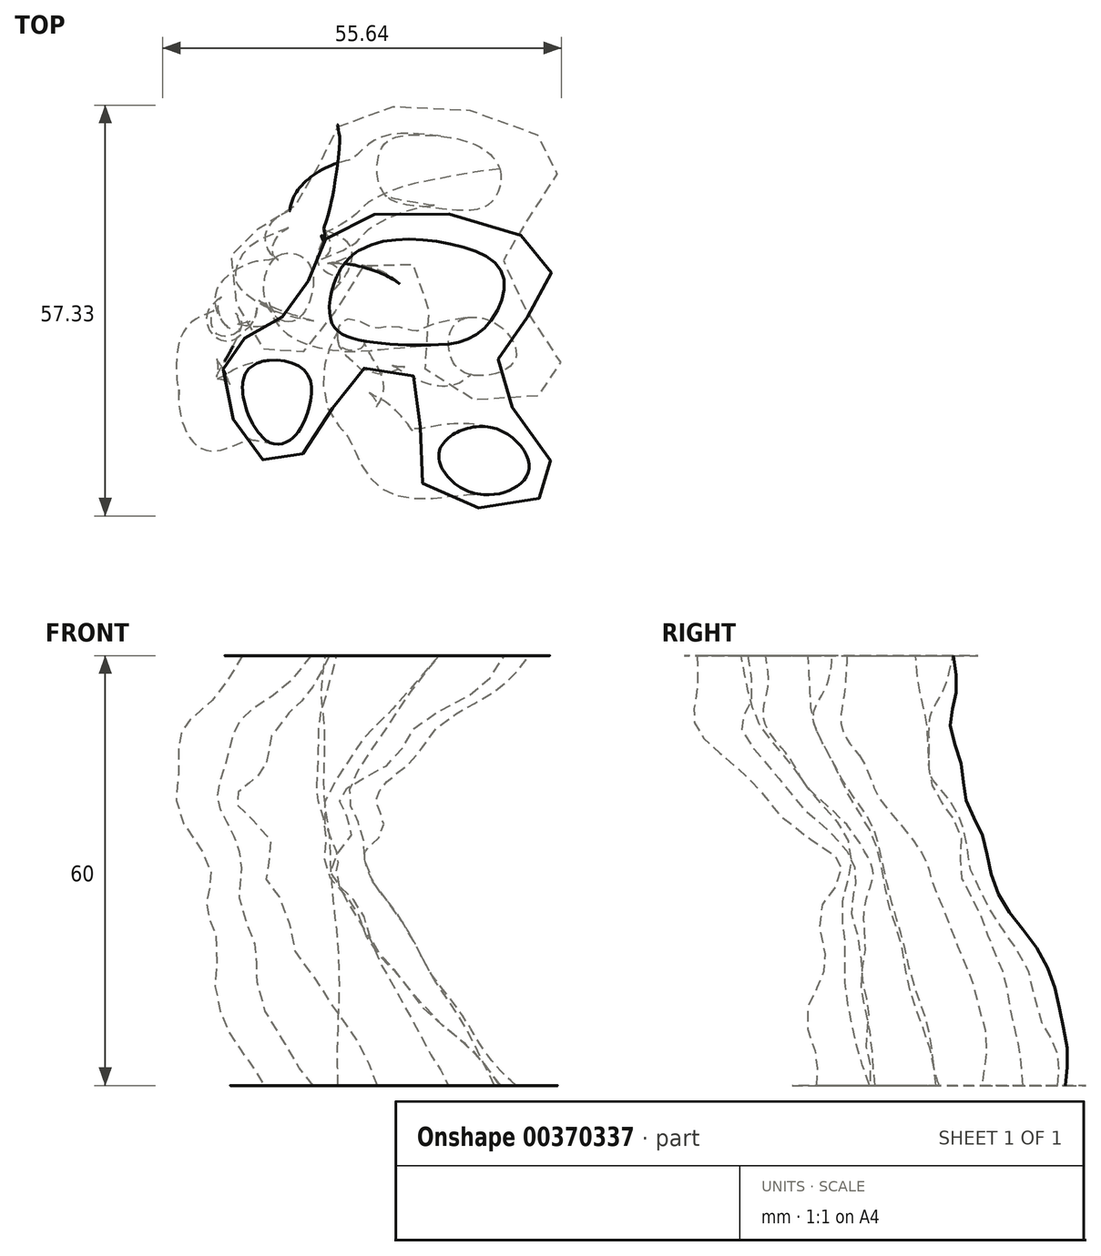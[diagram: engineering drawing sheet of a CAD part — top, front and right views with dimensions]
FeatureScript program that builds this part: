
annotation { "Feature Type Name" : "Feature", "Feature Type Description" : "" }
export const myFeature = defineFeature(function(context is Context, id is Id, definition is map)
    precondition{}
    {
        {
            var Q0;
            Q0=qCreatedBy(makeId("Top.planeOp"),FACE);
            cPlane(context, id + "F0", {"entities" : qUnion([Q0]), "cplaneType" : CPlaneType.OFFSET, "offset" : 5 * mm, "width" : 152.4 * mm, "height" : 152.4 * mm});
        }
        {
            var Q0;
            Q0=qCreatedBy(id+"F0.planeOp",FACE);
            var sketch = newSketch(context, id + "F1", { "sketchPlane" : qUnion([Q0])});
            skFitSpline(sketch, "E0", {"points": [v(-4.12, 24.5) * mm, v(12.71, 27.07) * mm, v(26.5, 20.1) * mm, v(22.26, 11.53) * mm, v(19.15, 3.69) * mm, v(26.98, -8.8) * mm, v(21.6, -13.7) * mm, v(8.13, -9.54) * mm, v(8.37, 3.2) * mm, v(0, 5.4) * mm, v(-6.08, -4.15) * mm, v(-12.69, -7.58) * mm, v(-18.32, 0) * mm, v(-18.32, 8.1) * mm, v(-12.69, 11.52) * mm, v(-7.54, 17.15) * mm, v(-4.12, 24.5) * mm]});
            skSolve(sketch);
        }
        {
            var Q0;
            Q0=qCreatedBy(id+"F0.planeOp",FACE);
            var sketch = newSketch(context, id + "F2", { "sketchPlane" : qUnion([Q0])});
            skFitSpline(sketch, "E1", {"points": [v(18.43, 18.57) * mm, v(16.76, 13.55) * mm, v(8.38, 13.27) * mm, v(2.23, 15.22) * mm, v(2.23, 21.92) * mm, v(8.1, 23.32) * mm, v(14.52, 22.2) * mm, v(18.43, 18.57) * mm]});
            skSolve(sketch);
        }
        {
            var Q0;
            Q0=qCreatedBy(id+"F0.planeOp",FACE);
            var sketch = newSketch(context, id + "F3", { "sketchPlane" : qUnion([Q0])});
            skFitSpline(sketch, "E2", {"points": [v(-12.55, 6.45) * mm, v(-8.36, 5.62) * mm, v(-8.08, 0.17) * mm, v(-10.88, -2.76) * mm, v(-14.23, 0.17) * mm, v(-12.55, 6.45) * mm]});
            skSolve(sketch);
        }
        {
            var Q0;
            Q0=qCreatedBy(id+"F0.planeOp",FACE);
            var sketch = newSketch(context, id + "F4", { "sketchPlane" : qUnion([Q0])});
            skFitSpline(sketch, "E3", {"points": [v(17.7, -2.86) * mm, v(20.7, -7.64) * mm, v(17.04, -10.13) * mm, v(12.22, -8.8) * mm, v(12.1, -3.14) * mm, v(17.7, -2.86) * mm]});
            skSolve(sketch);
        }
        {
            var Q0;
            Q0=qCreatedBy(id+"F0.planeOp",FACE);
            cPlane(context, id + "F5", {"entities" : qUnion([Q0]), "cplaneType" : CPlaneType.OFFSET, "offset" : 5 * mm, "width" : 152.4 * mm, "height" : 152.4 * mm});
        }
        {
            var Q0;
            Q0=qCreatedBy(id+"F5.planeOp",FACE);
            var sketch = newSketch(context, id + "F6", { "sketchPlane" : qUnion([Q0])});
            skFitSpline(sketch, "E4", {"points": [v(-7.05, 23.03) * mm, v(8.37, 25.24) * mm, v(21.1, 19.11) * mm, v(17.19, 11.52) * mm, v(14.74, 2.22) * mm, v(22.09, -9.05) * mm, v(17.19, -13.7) * mm, v(5.19, -10.27) * mm, v(5.43, 2.7) * mm, v(-3.38, 5.65) * mm, v(-10.48, -3.9) * mm, v(-16.85, -7.09) * mm, v(-20.77, 0) * mm, v(-20.28, 6.38) * mm, v(-14.9, 10.54) * mm, v(-10.48, 15.44) * mm, v(-7.05, 23.03) * mm]});
            skSolve(sketch);
        }
        {
            var Q0;
            Q0=qCreatedBy(id+"F5.planeOp",FACE);
            var sketch = newSketch(context, id + "F7", { "sketchPlane" : qUnion([Q0])});
            skFitSpline(sketch, "E5", {"points": [v(14.34, 18.87) * mm, v(13.14, 14.27) * mm, v(4.95, 14.07) * mm, v(0.15, 16.27) * mm, v(0, 21.86) * mm, v(7.15, 23.06) * mm, v(11.74, 21.66) * mm, v(14.34, 18.87) * mm]});
            skSolve(sketch);
        }
        {
            var Q0;
            Q0=qCreatedBy(id+"F5.planeOp",FACE);
            var sketch = newSketch(context, id + "F8", { "sketchPlane" : qUnion([Q0])});
            skFitSpline(sketch, "E6", {"points": [v(-16, 5.31) * mm, v(-11.56, 4.66) * mm, v(-12.52, -2) * mm, v(-15.68, -3.16) * mm, v(-17.67, 0) * mm, v(-16, 5.31) * mm]});
            skSolve(sketch);
        }
        {
            var Q0;
            Q0=qCreatedBy(id+"F5.planeOp",FACE);
            var sketch = newSketch(context, id + "F9", { "sketchPlane" : qUnion([Q0])});
            skFitSpline(sketch, "E7", {"points": [v(13.75, -3) * mm, v(16.15, -7.8) * mm, v(13.55, -10.39) * mm, v(9.07, -8.97) * mm, v(9.35, -3.6) * mm, v(13.75, -3) * mm]});
            skSolve(sketch);
        }
        {
            var Q0;
            Q0=qCreatedBy(id+"F5.planeOp",FACE);
            cPlane(context, id + "F10", {"entities" : qUnion([Q0]), "cplaneType" : CPlaneType.OFFSET, "offset" : 5 * mm, "width" : 152.4 * mm, "height" : 152.4 * mm});
        }
        {
            var Q0;
            Q0=qCreatedBy(id+"F10.planeOp",FACE);
            var sketch = newSketch(context, id + "F11", { "sketchPlane" : qUnion([Q0])});
            skFitSpline(sketch, "E8", {"points": [v(-8.03, 22.05) * mm, v(5.92, 23.28) * mm, v(15.47, 18.38) * mm, v(13.27, 11.03) * mm, v(11.56, 1) * mm, v(17.43, -8.8) * mm, v(13.02, -13.7) * mm, v(2.99, -10.76) * mm, v(3.47, 1.24) * mm, v(-4.85, 4.42) * mm, v(-12.2, -2.2) * mm, v(-17.83, -7.58) * mm, v(-21.5, -4.15) * mm, v(-22.73, 4.67) * mm, v(-17.58, 9.56) * mm, v(-12.2, 13.73) * mm, v(-8.03, 22.05) * mm]});
            skSolve(sketch);
        }
        {
            var Q0;
            Q0=qCreatedBy(id+"F10.planeOp",FACE);
            var sketch = newSketch(context, id + "F12", { "sketchPlane" : qUnion([Q0])});
            skFitSpline(sketch, "E9", {"points": [v(8.55, 15.27) * mm, v(6.55, 13.07) * mm, v(0, 13.07) * mm, v(-3.84, 15.47) * mm, v(-3.24, 19.27) * mm, v(2.75, 20.67) * mm, v(7.55, 19.07) * mm, v(8.55, 15.27) * mm]});
            skSolve(sketch);
        }
        {
            var Q0;
            Q0=qCreatedBy(id+"F10.planeOp",FACE);
            var sketch = newSketch(context, id + "F13", { "sketchPlane" : qUnion([Q0])});
            skFitSpline(sketch, "E10", {"points": [v(-19.66, 3.4) * mm, v(-15.66, 4.4) * mm, v(-14.46, -1) * mm, v(-18.17, -3) * mm, v(-20, -1.66) * mm, v(-19.66, 3.4) * mm]});
            skSolve(sketch);
        }
        {
            var Q0;
            Q0=qCreatedBy(id+"F10.planeOp",FACE);
            var sketch = newSketch(context, id + "F14", { "sketchPlane" : qUnion([Q0])});
            skFitSpline(sketch, "E11", {"points": [v(11.07, -3.7) * mm, v(13.06, -8.3) * mm, v(11.9, -11.3) * mm, v(6.9, -10.3) * mm, v(6.67, -4.5) * mm, v(11.07, -3.7) * mm]});
            skSolve(sketch);
        }
        {
            var Q0;
            Q0=qCreatedBy(id+"F10.planeOp",FACE);
            cPlane(context, id + "F15", {"entities" : qUnion([Q0]), "cplaneType" : CPlaneType.OFFSET, "offset" : 5 * mm, "width" : 152.4 * mm, "height" : 152.4 * mm});
        }
        {
            var Q0;
            Q0=qCreatedBy(id+"F15.planeOp",FACE);
            var sketch = newSketch(context, id + "F16", { "sketchPlane" : qUnion([Q0])});
            skFitSpline(sketch, "E12", {"points": [v(-9.5, 20.58) * mm, v(4.2, 21.8) * mm, v(12.05, 16.17) * mm, v(8.86, 9.07) * mm, v(8.37, 0) * mm, v(14.74, -6.35) * mm, v(7.88, -11.99) * mm, v(0, -8.56) * mm, v(1.52, 0) * mm, v(-6.08, 3.69) * mm, v(-10.97, 0) * mm, v(-13.91, -4.64) * mm, v(-20.03, -6.84) * mm, v(-22.73, 3.93) * mm, v(-17.34, 7.85) * mm, v(-13.42, 12.5) * mm, v(-9.5, 20.58) * mm]});
            skSolve(sketch);
        }
        {
            var Q0;
            Q0=qCreatedBy(id+"F15.planeOp",FACE);
            var sketch = newSketch(context, id + "F17", { "sketchPlane" : qUnion([Q0])});
            skFitSpline(sketch, "E13", {"points": [v(4.75, 15.47) * mm, v(2.75, 11.68) * mm, v(-3.44, 12.08) * mm, v(-7.04, 14.07) * mm, v(-6.64, 18.07) * mm, v(-1.6, 19.66) * mm, v(2.55, 18.87) * mm, v(4.75, 15.47) * mm]});
            skSolve(sketch);
        }
        {
            var Q0;
            Q0=qCreatedBy(id+"F15.planeOp",FACE);
            var sketch = newSketch(context, id + "F18", { "sketchPlane" : qUnion([Q0])});
            skFitSpline(sketch, "E14", {"points": [v(-20.9, 1.85) * mm, v(-16.93, 2.72) * mm, v(-15.5, -1.35) * mm, v(-17.3, -3.75) * mm, v(-20.1, -2.95) * mm, v(-20.9, 1.85) * mm]});
            skSolve(sketch);
        }
        {
            var Q0;
            Q0=qCreatedBy(id+"F15.planeOp",FACE);
            var sketch = newSketch(context, id + "F19", { "sketchPlane" : qUnion([Q0])});
            skFitSpline(sketch, "E15", {"points": [v(7.97, -4.39) * mm, v(9.17, -6.39) * mm, v(8.77, -8.58) * mm, v(3.78, -8.98) * mm, v(3.58, -4.99) * mm, v(7.97, -4.39) * mm]});
            skSolve(sketch);
        }
        {
            var Q0;
            Q0=qCreatedBy(id+"F15.planeOp",FACE);
            cPlane(context, id + "F20", {"entities" : qUnion([Q0]), "cplaneType" : CPlaneType.OFFSET, "offset" : 5 * mm, "width" : 152.4 * mm, "height" : 152.4 * mm});
        }
        {
            var Q0;
            Q0=qCreatedBy(id+"F20.planeOp",FACE);
            var sketch = newSketch(context, id + "F21", { "sketchPlane" : qUnion([Q0])});
            skFitSpline(sketch, "E16", {"points": [v(-13.18, 17.64) * mm, v(0, 19.11) * mm, v(6.66, 13.48) * mm, v(3.47, 8.58) * mm, v(4.2, 0) * mm, v(10.09, -5.37) * mm, v(7.64, -10.03) * mm, v(0, -10.76) * mm, v(-2.4, -1.95) * mm, v(-8.03, 0) * mm, v(-12.69, -1.95) * mm, v(-14.4, -5.86) * mm, v(-17.83, -8.31) * mm, v(-22.24, -3.41) * mm, v(-21.5, 4.18) * mm, v(-15.87, 9.8) * mm, v(-13.18, 17.64) * mm]});
            skSolve(sketch);
        }
        {
            var Q0;
            Q0=qCreatedBy(id+"F20.planeOp",FACE);
            var sketch = newSketch(context, id + "F22", { "sketchPlane" : qUnion([Q0])});
            skFitSpline(sketch, "E17", {"points": [v(0, 14.47) * mm, v(0, 10.08) * mm, v(-5.44, 9.48) * mm, v(-10.03, 11.48) * mm, v(-10.23, 14.87) * mm, v(-6.84, 16.87) * mm, v(-3.44, 16.67) * mm, v(0, 14.47) * mm]});
            skSolve(sketch);
        }
        {
            var Q0;
            Q0=qCreatedBy(id+"F20.planeOp",FACE);
            var sketch = newSketch(context, id + "F23", { "sketchPlane" : qUnion([Q0])});
            skFitSpline(sketch, "E18", {"points": [v(-20.77, 0.14) * mm, v(-17.77, 1.83) * mm, v(-15.78, -1.37) * mm, v(-17.57, -4.17) * mm, v(-19.77, -3.57) * mm, v(-20.77, 0.14) * mm]});
            skSolve(sketch);
        }
        {
            var Q0;
            Q0=qCreatedBy(id+"F20.planeOp",FACE);
            var sketch = newSketch(context, id + "F24", { "sketchPlane" : qUnion([Q0])});
            skFitSpline(sketch, "E19", {"points": [v(4.46, -3.62) * mm, v(6.46, -5.62) * mm, v(5.08, -8.97) * mm, v(1.46, -8.41) * mm, v(1.07, -4.22) * mm, v(4.46, -3.62) * mm]});
            skSolve(sketch);
        }
        {
            var Q0;
            Q0=qCreatedBy(id+"F20.planeOp",FACE);
            cPlane(context, id + "F25", {"entities" : qUnion([Q0]), "cplaneType" : CPlaneType.OFFSET, "offset" : 5 * mm, "width" : 152.4 * mm, "height" : 152.4 * mm});
        }
        {
            var Q0;
            Q0=qCreatedBy(id+"F25.planeOp",FACE);
            var sketch = newSketch(context, id + "F26", { "sketchPlane" : qUnion([Q0])});
            skFitSpline(sketch, "E20", {"points": [v(-12.82, 14.5) * mm, v(-2.24, 15.58) * mm, v(3.73, 10.96) * mm, v(0, 5.8) * mm, v(0, 0) * mm, v(6.45, -5.86) * mm, v(4.82, -10.74) * mm, v(-2.5, -11.29) * mm, v(-5.5, -3.15) * mm, v(-10.65, 0) * mm, v(-15.53, -3.15) * mm, v(-15.8, -6.4) * mm, v(-20.14, -8.03) * mm, v(-25.57, 0) * mm, v(-23.13, 2.82) * mm, v(-15.3, 8.02) * mm, v(-12.82, 14.5) * mm]});
            skSolve(sketch);
        }
        {
            var Q0;
            Q0=qCreatedBy(id+"F25.planeOp",FACE);
            var sketch = newSketch(context, id + "F27", { "sketchPlane" : qUnion([Q0])});
            skFitSpline(sketch, "E21", {"points": [v(-1.64, 11.88) * mm, v(-2.04, 8.08) * mm, v(-7.44, 7.68) * mm, v(-11.03, 9.48) * mm, v(-11.03, 12.67) * mm, v(-8.04, 13.67) * mm, v(-4.64, 13.07) * mm, v(-1.64, 11.88) * mm]});
            skSolve(sketch);
        }
        {
            var Q0;
            Q0=qCreatedBy(id+"F25.planeOp",FACE);
            var sketch = newSketch(context, id + "F28", { "sketchPlane" : qUnion([Q0])});
            skFitSpline(sketch, "E22", {"points": [v(-22.4, -1.58) * mm, v(-19.8, 0.41) * mm, v(-18, -1.78) * mm, v(-18.33, -4.99) * mm, v(-21, -4.99) * mm, v(-22.4, -1.58) * mm]});
            skSolve(sketch);
        }
        {
            var Q0;
            Q0=qCreatedBy(id+"F25.planeOp",FACE);
            var sketch = newSketch(context, id + "F29", { "sketchPlane" : qUnion([Q0])});
            skFitSpline(sketch, "E23", {"points": [v(1.34, -3.72) * mm, v(3.34, -6.92) * mm, v(2.34, -9.12) * mm, v(-1.44, -8.98) * mm, v(-2.06, -4.92) * mm, v(1.34, -3.72) * mm]});
            skSolve(sketch);
        }
        {
            var Q0;
            Q0=qCreatedBy(id+"F25.planeOp",FACE);
            cPlane(context, id + "F30", {"entities" : qUnion([Q0]), "cplaneType" : CPlaneType.OFFSET, "offset" : 5 * mm, "width" : 152.4 * mm, "height" : 152.4 * mm});
        }
        {
            var Q0;
            Q0=qCreatedBy(id+"F30.planeOp",FACE);
            var sketch = newSketch(context, id + "F31", { "sketchPlane" : qUnion([Q0])});
            skFitSpline(sketch, "E24", {"points": [v(-15.83, 12.08) * mm, v(-5.64, 14.07) * mm, v(0, 10.48) * mm, v(-2.24, 4.68) * mm, v(-1.84, 0) * mm, v(2.95, -4.5) * mm, v(2.35, -7.1) * mm, v(-5.44, -8.1) * mm, v(-6.84, 0) * mm, v(-11.23, 1.69) * mm, v(-15.23, -1.9) * mm, v(-15.83, -6.3) * mm, v(-20.62, -7.5) * mm, v(-23.82, -2.3) * mm, v(-23.02, 2.29) * mm, v(-18.02, 7.28) * mm, v(-15.83, 12.08) * mm]});
            skSolve(sketch);
        }
        {
            var Q0;
            Q0=qCreatedBy(id+"F30.planeOp",FACE);
            var sketch = newSketch(context, id + "F32", { "sketchPlane" : qUnion([Q0])});
            skFitSpline(sketch, "E25", {"points": [v(-6.24, 10.48) * mm, v(-5.44, 6.88) * mm, v(-9.83, 5.48) * mm, v(-13.43, 6.68) * mm, v(-14.23, 9.08) * mm, v(-12.63, 10.88) * mm, v(-8.84, 11.28) * mm, v(-6.24, 10.48) * mm]});
            skSolve(sketch);
        }
        {
            var Q0;
            Q0=qCreatedBy(id+"F30.planeOp",FACE);
            var sketch = newSketch(context, id + "F33", { "sketchPlane" : qUnion([Q0])});
            skFitSpline(sketch, "E26", {"points": [v(-21.53, -1.24) * mm, v(-18.93, -1.24) * mm, v(-17.53, -3.03) * mm, v(-18.53, -4.43) * mm, v(-21.13, -4.43) * mm, v(-21.53, -1.24) * mm]});
            skSolve(sketch);
        }
        {
            var Q0;
            Q0=qCreatedBy(id+"F30.planeOp",FACE);
            var sketch = newSketch(context, id + "F34", { "sketchPlane" : qUnion([Q0])});
            skFitSpline(sketch, "E27", {"points": [v(-2.64, -2.35) * mm, v(0, -4.55) * mm, v(-1.04, -6.55) * mm, v(-3.84, -6.15) * mm, v(-4.24, -3.95) * mm, v(-2.64, -2.35) * mm]});
            skSolve(sketch);
        }
        {
            var Q0;
            Q0=qCreatedBy(id+"F30.planeOp",FACE);
            cPlane(context, id + "F35", {"entities" : qUnion([Q0]), "cplaneType" : CPlaneType.OFFSET, "offset" : 5 * mm, "width" : 152.4 * mm, "height" : 152.4 * mm});
        }
        {
            var Q0;
            Q0=qCreatedBy(id+"F35.planeOp",FACE);
            var sketch = newSketch(context, id + "F36", { "sketchPlane" : qUnion([Q0])});
            skFitSpline(sketch, "E28", {"points": [v(-14.78, 11.48) * mm, v(-4.2, 12.57) * mm, v(1.77, 7.96) * mm, v(-1.97, 2.8) * mm, v(-1.97, -3) * mm, v(4.48, -8.87) * mm, v(2.85, -13.75) * mm, v(-4.47, -14.3) * mm, v(-7.46, -6.15) * mm, v(-12.61, -3) * mm, v(-17.5, -6.15) * mm, v(-17.77, -9.4) * mm, v(-22.11, -11.04) * mm, v(-27.54, -3) * mm, v(-25.1, -0.18) * mm, v(-17.27, 5.01) * mm, v(-14.78, 11.48) * mm]});
            skSolve(sketch);
        }
        {
            var Q0;
            Q0=qCreatedBy(id+"F35.planeOp",FACE);
            var sketch = newSketch(context, id + "F37", { "sketchPlane" : qUnion([Q0])});
            skFitSpline(sketch, "E29", {"points": [v(-2.27, 7.4) * mm, v(-4.04, 3.54) * mm, v(-9.01, 2.74) * mm, v(-12.86, 4.02) * mm, v(-13.98, 6.75) * mm, v(-12.06, 9.96) * mm, v(-5.48, 9.8) * mm, v(-2.27, 7.4) * mm]});
            skSolve(sketch);
        }
        {
            var Q0;
            Q0=qCreatedBy(id+"F35.planeOp",FACE);
            var sketch = newSketch(context, id + "F38", { "sketchPlane" : qUnion([Q0])});
            skFitSpline(sketch, "E30", {"points": [v(-24.32, -2.67) * mm, v(-19.66, -2.67) * mm, v(-18.7, -4.92) * mm, v(-19.57, -7.32) * mm, v(-23.03, -7.32) * mm, v(-24.32, -2.67) * mm]});
            skSolve(sketch);
        }
        {
            var Q0;
            Q0=qCreatedBy(id+"F35.planeOp",FACE);
            var sketch = newSketch(context, id + "F39", { "sketchPlane" : qUnion([Q0])});
            skFitSpline(sketch, "E31", {"points": [v(-2.5, -4.98) * mm, v(0.23, -7.25) * mm, v(1.7, -11.1) * mm, v(-3.03, -11.45) * mm, v(-5.13, -6.03) * mm, v(-2.5, -4.98) * mm]});
            skSolve(sketch);
        }
        {
            var Q0;
            Q0=qCreatedBy(id+"F35.planeOp",FACE);
            cPlane(context, id + "F40", {"entities" : qUnion([Q0]), "cplaneType" : CPlaneType.OFFSET, "offset" : 5 * mm, "width" : 152.4 * mm, "height" : 152.4 * mm});
        }
        {
            var Q0;
            Q0=qCreatedBy(id+"F40.planeOp",FACE);
            var sketch = newSketch(context, id + "F41", { "sketchPlane" : qUnion([Q0])});
            skFitSpline(sketch, "E32", {"points": [v(-18.89, 9) * mm, v(-5.71, 10.47) * mm, v(0.94, 4.84) * mm, v(-2.24, -0.06) * mm, v(-1.5, -8.65) * mm, v(4.37, -14.02) * mm, v(1.92, -18.67) * mm, v(-5.71, -19.4) * mm, v(-8.12, -10.6) * mm, v(-13.75, -8.65) * mm, v(-18.4, -10.6) * mm, v(-20.11, -14.5) * mm, v(-23.54, -16.96) * mm, v(-27.95, -12.06) * mm, v(-27.22, -4.47) * mm, v(-21.58, 1.16) * mm, v(-18.89, 9) * mm]});
            skSolve(sketch);
        }
        {
            var Q0;
            Q0=qCreatedBy(id+"F40.planeOp",FACE);
            var sketch = newSketch(context, id + "F42", { "sketchPlane" : qUnion([Q0])});
            skFitSpline(sketch, "E33", {"points": [v(-3.97, 4.35) * mm, v(-5.9, 0) * mm, v(-11.84, -1.25) * mm, v(-17.44, 1.72) * mm, v(-18.49, 3.82) * mm, v(-16.39, 7.5) * mm, v(-8.69, 7.5) * mm, v(-3.97, 4.35) * mm]});
            skSolve(sketch);
        }
        {
            var Q0;
            Q0=qCreatedBy(id+"F40.planeOp",FACE);
            var sketch = newSketch(context, id + "F43", { "sketchPlane" : qUnion([Q0])});
            skFitSpline(sketch, "E34", {"points": [v(-25.83, -5.62) * mm, v(-21.98, -5.62) * mm, v(-20.93, -9.47) * mm, v(-22.33, -12.8) * mm, v(-25.48, -12.8) * mm, v(-25.83, -5.62) * mm]});
            skSolve(sketch);
        }
        {
            var Q0;
            Q0=qCreatedBy(id+"F40.planeOp",FACE);
            var sketch = newSketch(context, id + "F44", { "sketchPlane" : qUnion([Q0])});
            skFitSpline(sketch, "E35", {"points": [v(-3.1, -10) * mm, v(1.28, -14.54) * mm, v(-2.4, -17.17) * mm, v(-5.37, -15.24) * mm, v(-5.37, -10.7) * mm, v(-3.1, -10) * mm]});
            skSolve(sketch);
        }
        {
            var Q0;
            Q0=qCreatedBy(id+"F40.planeOp",FACE);
            cPlane(context, id + "F45", {"entities" : qUnion([Q0]), "cplaneType" : CPlaneType.OFFSET, "offset" : 5 * mm, "width" : 152.4 * mm, "height" : 152.4 * mm});
        }
        {
            var Q0;
            Q0=qCreatedBy(id+"F45.planeOp",FACE);
            var sketch = newSketch(context, id + "F46", { "sketchPlane" : qUnion([Q0])});
            skFitSpline(sketch, "E36", {"points": [v(-14.52, 7.84) * mm, v(-0.8, 9.06) * mm, v(7.03, 3.43) * mm, v(3.84, -3.67) * mm, v(3.35, -12.75) * mm, v(9.72, -19.1) * mm, v(2.86, -24.73) * mm, v(-5.02, -21.3) * mm, v(-3.5, -12.75) * mm, v(-11.1, -9.06) * mm, v(-16, -12.75) * mm, v(-18.93, -17.38) * mm, v(-25.05, -19.59) * mm, v(-27.74, -8.81) * mm, v(-22.36, -4.9) * mm, v(-18.44, -0.24) * mm, v(-14.52, 7.84) * mm]});
            skSolve(sketch);
        }
        {
            var Q0;
            Q0=qCreatedBy(id+"F45.planeOp",FACE);
            var sketch = newSketch(context, id + "F47", { "sketchPlane" : qUnion([Q0])});
            skFitSpline(sketch, "E37", {"points": [v(3.03, 2.6) * mm, v(0, -2.82) * mm, v(-6.77, -3.35) * mm, v(-12.01, -2.3) * mm, v(-14.11, 1.55) * mm, v(-12.19, 4.17) * mm, v(-3.1, 5.4) * mm, v(3.03, 2.6) * mm]});
            skSolve(sketch);
        }
        {
            var Q0;
            Q0=qCreatedBy(id+"F45.planeOp",FACE);
            var sketch = newSketch(context, id + "F48", { "sketchPlane" : qUnion([Q0])});
            skFitSpline(sketch, "E38", {"points": [v(-25.13, -8.77) * mm, v(-20.58, -8.77) * mm, v(-19.88, -13.32) * mm, v(-21.28, -16.47) * mm, v(-25.13, -16.47) * mm, v(-25.13, -8.77) * mm]});
            skSolve(sketch);
        }
        {
            var Q0;
            Q0=qCreatedBy(id+"F45.planeOp",FACE);
            var sketch = newSketch(context, id + "F49", { "sketchPlane" : qUnion([Q0])});
            skFitSpline(sketch, "E39", {"points": [v(1.8, -13.67) * mm, v(5.83, -19.8) * mm, v(2.16, -22.07) * mm, v(-1.87, -20.32) * mm, v(-2.57, -15.94) * mm, v(1.8, -13.67) * mm]});
            skSolve(sketch);
        }
        {
            var Q0;
            Q0=qCreatedBy(id+"F45.planeOp",FACE);
            cPlane(context, id + "F50", {"entities" : qUnion([Q0]), "cplaneType" : CPlaneType.OFFSET, "offset" : 5 * mm, "width" : 152.4 * mm, "height" : 152.4 * mm});
        }
        {
            var Q0;
            Q0=qCreatedBy(id+"F50.planeOp",FACE);
            var sketch = newSketch(context, id + "F51", { "sketchPlane" : qUnion([Q0])});
            skFitSpline(sketch, "E40", {"points": [v(-12.26, 6.45) * mm, v(1.7, 7.68) * mm, v(11.25, 2.78) * mm, v(9.05, -4.57) * mm, v(7.33, -14.6) * mm, v(13.2, -24.4) * mm, v(8.8, -29.3) * mm, v(-1.24, -26.36) * mm, v(-0.75, -14.36) * mm, v(-9.07, -11.18) * mm, v(-16.42, -17.8) * mm, v(-22.05, -23.18) * mm, v(-25.73, -19.75) * mm, v(-26.95, -10.93) * mm, v(-21.8, -6.04) * mm, v(-16.42, -1.87) * mm, v(-12.26, 6.45) * mm]});
            skSolve(sketch);
        }
        {
            var Q0;
            Q0=qCreatedBy(id+"F50.planeOp",FACE);
            var sketch = newSketch(context, id + "F52", { "sketchPlane" : qUnion([Q0])});
            skFitSpline(sketch, "E41", {"points": [v(6.58, 0) * mm, v(4.42, -3.99) * mm, v(-2.06, -6.65) * mm, v(-10.03, -5.15) * mm, v(-12.85, -1.17) * mm, v(-8.54, 4.65) * mm, v(1.76, 4.15) * mm, v(6.58, 0) * mm]});
            skSolve(sketch);
        }
        {
            var Q0;
            Q0=qCreatedBy(id+"F50.planeOp",FACE);
            var sketch = newSketch(context, id + "F53", { "sketchPlane" : qUnion([Q0])});
            skFitSpline(sketch, "E42", {"points": [v(-24.98, -11.63) * mm, v(-19, -11.63) * mm, v(-19.16, -17.77) * mm, v(-20.5, -20.26) * mm, v(-23.15, -20.26) * mm, v(-24.98, -11.63) * mm]});
            skSolve(sketch);
        }
        {
            var Q0;
            Q0=qCreatedBy(id+"F50.planeOp",FACE);
            var sketch = newSketch(context, id + "F54", { "sketchPlane" : qUnion([Q0])});
            skFitSpline(sketch, "E43", {"points": [v(5.25, -17.27) * mm, v(9.73, -23.75) * mm, v(7.29, -26.68) * mm, v(2.26, -26.08) * mm, v(1.26, -20.1) * mm, v(5.25, -17.27) * mm]});
            skSolve(sketch);
        }
        {
            var Q0;
            Q0=qCreatedBy(id+"F50.planeOp",FACE);
            cPlane(context, id + "F55", {"entities" : qUnion([Q0]), "cplaneType" : CPlaneType.OFFSET, "offset" : 5 * mm, "width" : 152.4 * mm, "height" : 152.4 * mm});
        }
        {
            var Q0;
            Q0=qCreatedBy(id+"F55.planeOp",FACE);
            var sketch = newSketch(context, id + "F56", { "sketchPlane" : qUnion([Q0])});
            skFitSpline(sketch, "E44", {"points": [v(-7.93, 8.21) * mm, v(7.5, 10.41) * mm, v(20.23, 4.3) * mm, v(16.31, -3.3) * mm, v(13.86, -12.6) * mm, v(21.2, -23.87) * mm, v(16.31, -28.52) * mm, v(4.31, -25.1) * mm, v(4.56, -12.11) * mm, v(-4.26, -9.18) * mm, v(-11.36, -18.73) * mm, v(-17.73, -21.9) * mm, v(-21.64, -14.82) * mm, v(-21.15, -8.44) * mm, v(-15.77, -4.28) * mm, v(-11.36, 0.62) * mm, v(-7.93, 8.21) * mm]});
            skSolve(sketch);
        }
        {
            var Q0;
            Q0=qCreatedBy(id+"F55.planeOp",FACE);
            var sketch = newSketch(context, id + "F57", { "sketchPlane" : qUnion([Q0])});
            skFitSpline(sketch, "E45", {"points": [v(15.05, 1.66) * mm, v(11.72, -3) * mm, v(6.08, -6.15) * mm, v(-3.47, -5.14) * mm, v(-8.04, -2) * mm, v(-3.72, 5.8) * mm, v(8.4, 6.3) * mm, v(15.05, 1.66) * mm]});
            skSolve(sketch);
        }
        {
            var Q0;
            Q0=qCreatedBy(id+"F55.planeOp",FACE);
            var sketch = newSketch(context, id + "F58", { "sketchPlane" : qUnion([Q0])});
            skFitSpline(sketch, "E46", {"points": [v(-20, -10.47) * mm, v(-13.68, -10.47) * mm, v(-12.85, -16.44) * mm, v(-14.68, -18.6) * mm, v(-18.17, -18.6) * mm, v(-20, -10.47) * mm]});
            skSolve(sketch);
        }
        {
            var Q0;
            Q0=qCreatedBy(id+"F55.planeOp",FACE);
            var sketch = newSketch(context, id + "F59", { "sketchPlane" : qUnion([Q0])});
            skFitSpline(sketch, "E47", {"points": [v(12.5, -17.31) * mm, v(17.7, -23.92) * mm, v(14.53, -26.72) * mm, v(7.9, -25.41) * mm, v(5.91, -20.1) * mm, v(12.5, -17.31) * mm]});
            skSolve(sketch);
        }
        {
            var Q0;
            Q0=qCreatedBy(id+"F55.planeOp",FACE);
            cPlane(context, id + "F60", {"entities" : qUnion([Q0]), "cplaneType" : CPlaneType.OFFSET, "offset" : 5 * mm, "width" : 152.4 * mm, "height" : 152.4 * mm});
        }
        {
            var Q0;
            Q0=qCreatedBy(id+"F60.planeOp",FACE);
            var sketch = newSketch(context, id + "F61", { "sketchPlane" : qUnion([Q0])});
            skFitSpline(sketch, "E48", {"points": [v(-5.1, 9.67) * mm, v(11.73, 12.24) * mm, v(25.52, 5.26) * mm, v(21.28, -3.3) * mm, v(18.17, -11.14) * mm, v(26, -23.63) * mm, v(20.62, -28.53) * mm, v(7.15, -24.37) * mm, v(7.4, -11.63) * mm, v(-0.98, -9.43) * mm, v(-7.05, -18.98) * mm, v(-13.66, -22.4) * mm, v(-19.3, -14.83) * mm, v(-19.3, -6.74) * mm, v(-13.66, -3.3) * mm, v(-8.52, 2.33) * mm, v(-5.1, 9.67) * mm]});
            skSolve(sketch);
        }
        {
            var Q0;
            Q0=qCreatedBy(id+"F60.planeOp",FACE);
            var sketch = newSketch(context, id + "F62", { "sketchPlane" : qUnion([Q0])});
            skFitSpline(sketch, "E49", {"points": [v(18.87, 3.82) * mm, v(15.88, -3.99) * mm, v(8.24, -5.98) * mm, v(-2.22, -4.99) * mm, v(-5.21, -2.16) * mm, v(-2.4, 6.3) * mm, v(9.73, 8.47) * mm, v(18.87, 3.82) * mm]});
            skSolve(sketch);
        }
        {
            var Q0;
            Q0=qCreatedBy(id+"F60.planeOp",FACE);
            var sketch = newSketch(context, id + "F63", { "sketchPlane" : qUnion([Q0])});
            skFitSpline(sketch, "E50", {"points": [v(-16.84, -9.64) * mm, v(-8.7, -9.64) * mm, v(-8.87, -16.61) * mm, v(-10.86, -19.27) * mm, v(-14.18, -19.27) * mm, v(-16.84, -9.64) * mm]});
            skSolve(sketch);
        }
        {
            var Q0;
            Q0=qCreatedBy(id+"F60.planeOp",FACE);
            var sketch = newSketch(context, id + "F64", { "sketchPlane" : qUnion([Q0])});
            skFitSpline(sketch, "E51", {"points": [v(17.04, -17.44) * mm, v(22.52, -22.59) * mm, v(19.86, -26.24) * mm, v(13.05, -25.9) * mm, v(10.06, -20.6) * mm, v(17.04, -17.44) * mm]});
            skSolve(sketch);
        }
        {
            var Q0;
            Q0 = qSketchRegion(id + "F1", true);
            var Q1;
            Q1 = qSketchRegion(id + "F6", true);
            var Q2;
            Q2 = qSketchRegion(id + "F11", true);
            var Q3;
            Q3 = qSketchRegion(id + "F16", true);
            var Q4;
            Q4 = qSketchRegion(id + "F21", true);
            var Q5;
            Q5 = qSketchRegion(id + "F26", true);
            var Q6;
            Q6 = qSketchRegion(id + "F31", true);
            var Q7;
            Q7 = qSketchRegion(id + "F36", true);
            var Q8;
            Q8 = qSketchRegion(id + "F41", true);
            var Q9;
            Q9 = qSketchRegion(id + "F46", true);
            var Q10;
            Q10 = qSketchRegion(id + "F51", true);
            var Q11;
            Q11 = qSketchRegion(id + "F56", true);
            var Q12;
            Q12 = qSketchRegion(id + "F61", true);
            loft(context, id + "F65", {"sheetProfilesArray" : [{ "sheetProfileEntities" : qUnion([Q0]) }, { "sheetProfileEntities" : qUnion([Q1]) }, { "sheetProfileEntities" : qUnion([Q2]) }, { "sheetProfileEntities" : qUnion([Q3]) }, { "sheetProfileEntities" : qUnion([Q4]) }, { "sheetProfileEntities" : qUnion([Q5]) }, { "sheetProfileEntities" : qUnion([Q6]) }, { "sheetProfileEntities" : qUnion([Q7]) }, { "sheetProfileEntities" : qUnion([Q8]) }, { "sheetProfileEntities" : qUnion([Q9]) }, { "sheetProfileEntities" : qUnion([Q10]) }, { "sheetProfileEntities" : qUnion([Q11]) }, { "sheetProfileEntities" : qUnion([Q12]) }]});
        }
        {
            var Q1;
            Q1 = qSketchRegion(id + "F2", true);
            var Q2;
            Q2 = qSketchRegion(id + "F7", true);
            var Q3;
            Q3 = qSketchRegion(id + "F12", true);
            var Q4;
            Q4 = qSketchRegion(id + "F17", true);
            var Q5;
            Q5 = qSketchRegion(id + "F22", true);
            var Q6;
            Q6 = qSketchRegion(id + "F27", true);
            var Q7;
            Q7 = qSketchRegion(id + "F32", true);
            var Q8;
            Q8 = qSketchRegion(id + "F37", true);
            var Q9;
            Q9 = qSketchRegion(id + "F42", true);
            var Q10;
            Q10 = qSketchRegion(id + "F47", true);
            var Q11;
            Q11 = qSketchRegion(id + "F52", true);
            var Q12;
            Q12 = qSketchRegion(id + "F57", true);
            var Q13;
            Q13 = qSketchRegion(id + "F62", true);
            loft(context, id + "F66", {"operationType" : NewBodyOperationType.REMOVE, "sheetProfilesArray" : [{ "sheetProfileEntities" : qUnion([Q1]) }, { "sheetProfileEntities" : qUnion([Q2]) }, { "sheetProfileEntities" : qUnion([Q3]) }, { "sheetProfileEntities" : qUnion([Q4]) }, { "sheetProfileEntities" : qUnion([Q5]) }, { "sheetProfileEntities" : qUnion([Q6]) }, { "sheetProfileEntities" : qUnion([Q7]) }, { "sheetProfileEntities" : qUnion([Q8]) }, { "sheetProfileEntities" : qUnion([Q9]) }, { "sheetProfileEntities" : qUnion([Q10]) }, { "sheetProfileEntities" : qUnion([Q11]) }, { "sheetProfileEntities" : qUnion([Q12]) }, { "sheetProfileEntities" : qUnion([Q13]) }]});
        }
        {
            var Q1;
            Q1 = qSketchRegion(id + "F3", true);
            var Q2;
            Q2 = qSketchRegion(id + "F8", true);
            var Q3;
            Q3 = qSketchRegion(id + "F13", true);
            var Q4;
            Q4 = qSketchRegion(id + "F18", true);
            var Q5;
            Q5 = qSketchRegion(id + "F23", true);
            var Q6;
            Q6 = qSketchRegion(id + "F28", true);
            var Q7;
            Q7 = qSketchRegion(id + "F33", true);
            var Q8;
            Q8 = qSketchRegion(id + "F38", true);
            var Q9;
            Q9 = qSketchRegion(id + "F43", true);
            var Q10;
            Q10 = qSketchRegion(id + "F48", true);
            var Q11;
            Q11 = qSketchRegion(id + "F53", true);
            var Q12;
            Q12 = qSketchRegion(id + "F58", true);
            var Q13;
            Q13 = qSketchRegion(id + "F63", true);
            loft(context, id + "F67", {"operationType" : NewBodyOperationType.REMOVE, "sheetProfilesArray" : [{ "sheetProfileEntities" : qUnion([Q1]) }, { "sheetProfileEntities" : qUnion([Q2]) }, { "sheetProfileEntities" : qUnion([Q3]) }, { "sheetProfileEntities" : qUnion([Q4]) }, { "sheetProfileEntities" : qUnion([Q5]) }, { "sheetProfileEntities" : qUnion([Q6]) }, { "sheetProfileEntities" : qUnion([Q7]) }, { "sheetProfileEntities" : qUnion([Q8]) }, { "sheetProfileEntities" : qUnion([Q9]) }, { "sheetProfileEntities" : qUnion([Q10]) }, { "sheetProfileEntities" : qUnion([Q11]) }, { "sheetProfileEntities" : qUnion([Q12]) }, { "sheetProfileEntities" : qUnion([Q13]) }]});
        }
        {
            var Q1;
            Q1 = qSketchRegion(id + "F4", true);
            var Q2;
            Q2 = qSketchRegion(id + "F9", true);
            var Q3;
            Q3 = qSketchRegion(id + "F14", true);
            var Q4;
            Q4 = qSketchRegion(id + "F19", true);
            var Q5;
            Q5 = qSketchRegion(id + "F24", true);
            var Q6;
            Q6 = qSketchRegion(id + "F29", true);
            var Q7;
            Q7 = qSketchRegion(id + "F34", true);
            var Q8;
            Q8 = qSketchRegion(id + "F39", true);
            var Q9;
            Q9 = qSketchRegion(id + "F44", true);
            var Q10;
            Q10 = qSketchRegion(id + "F49", true);
            var Q11;
            Q11 = qSketchRegion(id + "F54", true);
            var Q12;
            Q12 = qSketchRegion(id + "F59", true);
            var Q13;
            Q13 = qSketchRegion(id + "F64", true);
            loft(context, id + "F68", {"operationType" : NewBodyOperationType.REMOVE, "sheetProfilesArray" : [{ "sheetProfileEntities" : qUnion([Q1]) }, { "sheetProfileEntities" : qUnion([Q2]) }, { "sheetProfileEntities" : qUnion([Q3]) }, { "sheetProfileEntities" : qUnion([Q4]) }, { "sheetProfileEntities" : qUnion([Q5]) }, { "sheetProfileEntities" : qUnion([Q6]) }, { "sheetProfileEntities" : qUnion([Q7]) }, { "sheetProfileEntities" : qUnion([Q8]) }, { "sheetProfileEntities" : qUnion([Q9]) }, { "sheetProfileEntities" : qUnion([Q10]) }, { "sheetProfileEntities" : qUnion([Q11]) }, { "sheetProfileEntities" : qUnion([Q12]) }, { "sheetProfileEntities" : qUnion([Q13]) }]});
        }
    });
